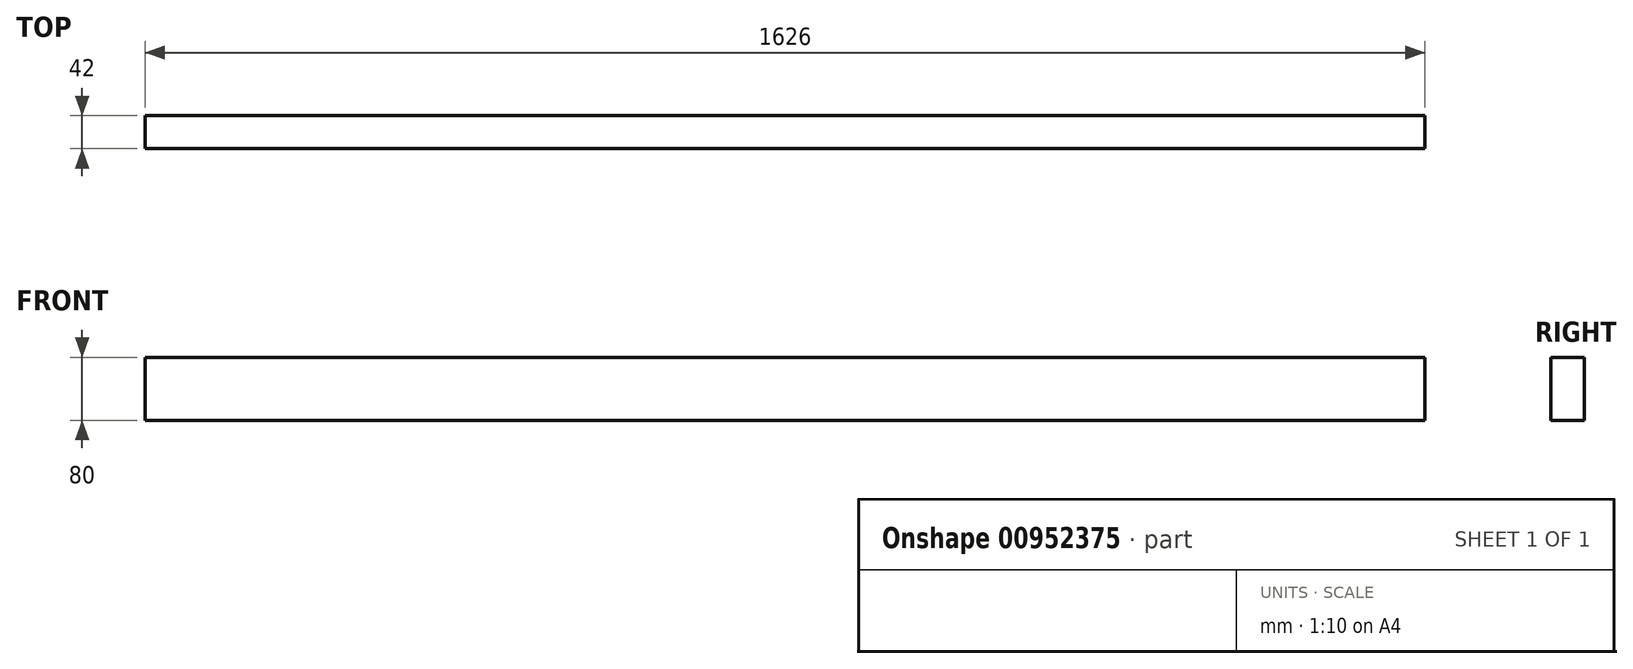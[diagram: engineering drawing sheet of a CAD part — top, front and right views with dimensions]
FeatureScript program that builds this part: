
annotation { "Feature Type Name" : "Feature", "Feature Type Description" : "" }
export const myFeature = defineFeature(function(context is Context, id is Id, definition is map)
    precondition{}
    {
        {
            var Q0;
            Q0=qCreatedBy(makeId("Front.planeOp"),FACE);
            var sketch = newSketch(context, id + "F0", { "sketchPlane" : qUnion([Q0])});
            skLineSegment(sketch, "E0.bottom", {"start": v(813, -40) * mm, "end": v(-813, -40) * mm});
            skLineSegment(sketch, "E0.top", {"start": v(813, 40) * mm, "end": v(-813, 40) * mm});
            skLineSegment(sketch, "E0.left", {"start": v(813, -40) * mm, "end": v(813, 40) * mm});
            skLineSegment(sketch, "E0.right", {"start": v(-813, -40) * mm, "end": v(-813, 40) * mm});
            skPoint(sketch, "E0.middle", {"position": v(0, 0) * mm});
            skSolve(sketch);
        }
        {
            var Q0;
            Q0=makeQuery(id+"F0.imprint","IMPRINT",FACE,{"disambiguationData":[TD([[makeQuery(id+"F0.imprint","IMPRINT",EDGE,{"derivedFrom":sQuery(id+"F0.wireOp",EDGE,"E0.bottom")}),-1.0]])]});
            extrude(context, id + "F1", {"entities" : qUnion([Q0]), "depth" : 42 * mm, "offsetDistance" : 25 * mm});
        }
    });
